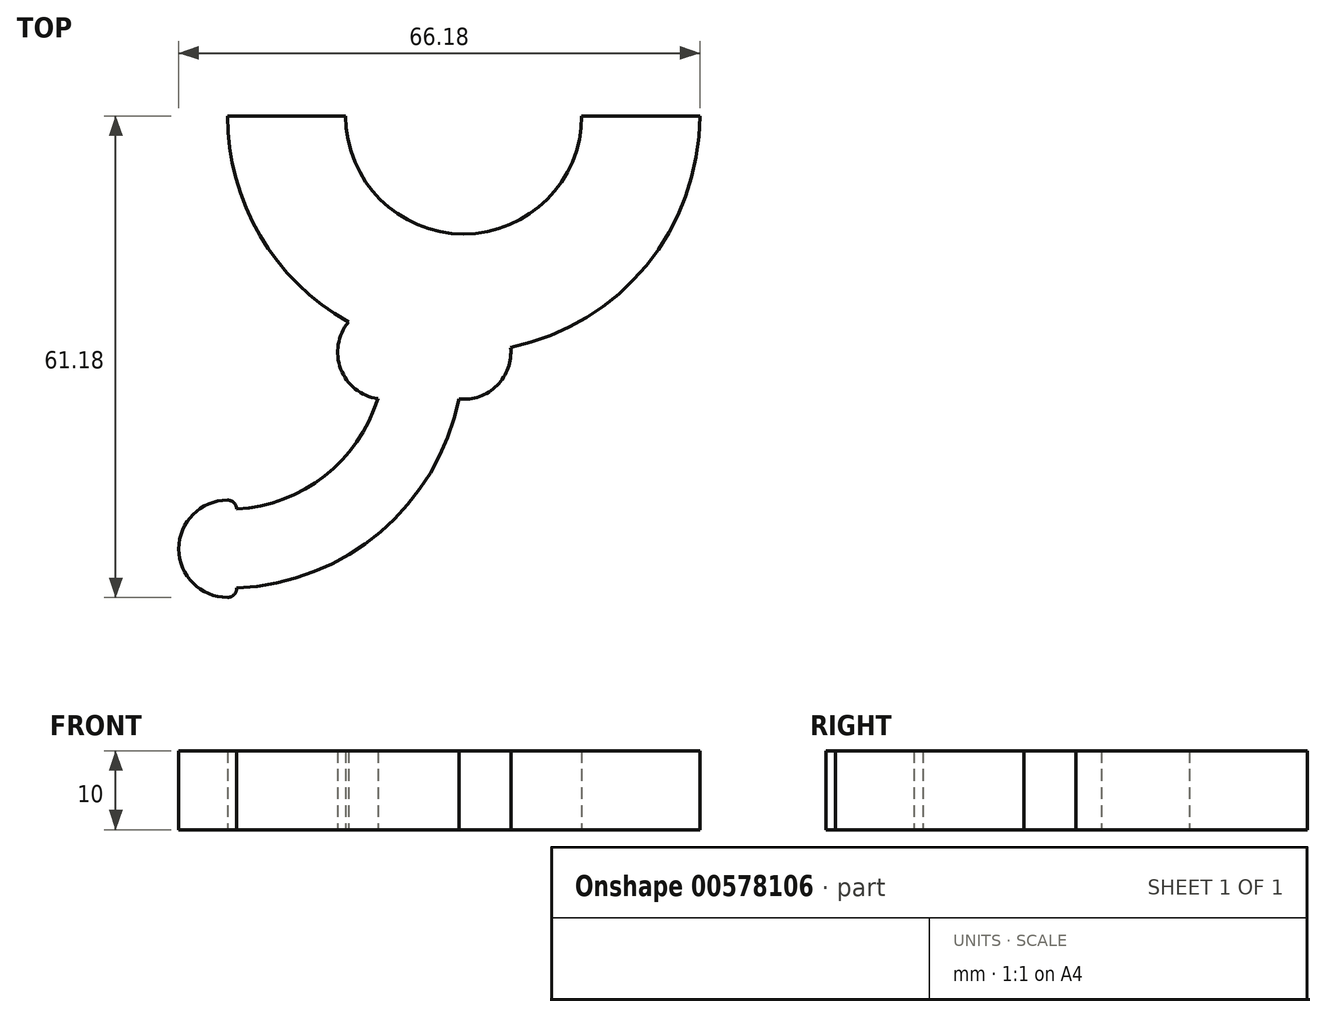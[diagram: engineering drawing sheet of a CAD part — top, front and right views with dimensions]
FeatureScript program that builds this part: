
annotation { "Feature Type Name" : "Feature", "Feature Type Description" : "" }
export const myFeature = defineFeature(function(context is Context, id is Id, definition is map)
    precondition{}
    {
        {
            var Q0;
            Q0=qCreatedBy(makeId("Top.planeOp"),FACE);
            var sketch = newSketch(context, id + "F0", { "sketchPlane" : qUnion([Q0])});
            skArc(sketch, "E0", {"start": v(15, 0) * mm, "mid": v(0, 15) * mm, "end": v(-15, 0) * mm});
            skLineSegment(sketch, "E1", {"start": v(30, 50) * mm, "end": v(30, 60) * mm});
            skLineSegment(sketch, "E2", {"start": v(30, 60) * mm, "end": v(30, 60) * mm});
            skArc(sketch, "E3", {"start": v(-5.97, 29.4) * mm, "mid": v(-23.23, 18.99) * mm, "end": v(-30, 0) * mm});
            skArc(sketch, "E4", {"start": v(30, 0) * mm, "mid": v(25.87, 15.18) * mm, "end": v(14.63, 26.19) * mm});
            skArc(sketch, "E5", {"start": v(28.82, 59.98) * mm, "mid": v(10.56, 52.85) * mm, "end": v(0.6, 35.97) * mm});
            skLineSegment(sketch, "E6", {"start": v(0, 30) * mm, "end": v(0, 30) * mm});
            skArc(sketch, "E7", {"start": v(28.82, 49.97) * mm, "mid": v(17.67, 45.75) * mm, "end": v(10.9, 35.93) * mm});
            skArc(sketch, "E8", {"start": v(4, 30) * mm, "mid": v(4, 29.87) * mm, "end": v(4, 29.73) * mm});
            skPoint(sketch, "E9.start.orphan", {"position": v(-28.8, -1.58) * mm});
            skArc(sketch, "E10.trimOffspring", {"start": v(0.6, 35.97) * mm, "mid": v(-4.24, 34.24) * mm, "end": v(-5.97, 29.4) * mm});
            skArc(sketch, "E11.trimOffspring", {"start": v(14.63, 26.19) * mm, "mid": v(15.6, 32.15) * mm, "end": v(10.9, 35.93) * mm});
            skArc(sketch, "E12", {"start": v(30, 48.82) * mm, "mid": v(36.18, 55) * mm, "end": v(30, 61.18) * mm});
            skArc(sketch, "E13", {"start": v(30, 61.18) * mm, "mid": v(29.16, 60.82) * mm, "end": v(28.82, 59.98) * mm});
            skArc(sketch, "E14", {"start": v(28.82, 49.97) * mm, "mid": v(29.18, 49.16) * mm, "end": v(30, 48.82) * mm});
            skLineSegment(sketch, "E15", {"start": v(-30, 0) * mm, "end": v(-15, 0) * mm});
            skLineSegment(sketch, "E16.trimOffspring", {"start": v(15, 0) * mm, "end": v(30, 0) * mm});
            skLineSegment(sketch, "E17.MirrorCS", {"start": v(0, -30) * mm, "end": v(0, -30) * mm});
            skLineSegment(sketch, "E18", {"start": v(-30, 0.02) * mm, "end": v(-15, 0.02) * mm});
            skLineSegment(sketch, "E19", {"start": v(15, 0.02) * mm, "end": v(30, 0.02) * mm});
            skArc(sketch, "E20.MirrorCS", {"start": v(-30, -61.16) * mm, "mid": v(-29.16, -60.8) * mm, "end": v(-28.82, -59.96) * mm});
            skArc(sketch, "E21.MirrorCS", {"start": v(-30, -48.8) * mm, "mid": v(-36.18, -54.98) * mm, "end": v(-30, -61.16) * mm});
            skArc(sketch, "E22.MirrorCS", {"start": v(-4, -29.98) * mm, "mid": v(-4, -29.85) * mm, "end": v(-4, -29.71) * mm});
            skArc(sketch, "E23.MirrorCS", {"start": v(-28.82, -49.95) * mm, "mid": v(-29.18, -49.14) * mm, "end": v(-30, -48.8) * mm});
            skLineSegment(sketch, "E24.MirrorCS", {"start": v(-30, -49.98) * mm, "end": v(-30, -59.98) * mm});
            skArc(sketch, "E25.MirrorCS", {"start": v(-0.6, -35.95) * mm, "mid": v(4.24, -34.22) * mm, "end": v(5.97, -29.38) * mm});
            skArc(sketch, "E26.MirrorCS", {"start": v(-30, 0.02) * mm, "mid": v(-25.87, -15.16) * mm, "end": v(-14.63, -26.17) * mm});
            skArc(sketch, "E27.MirrorCS", {"start": v(5.97, -29.38) * mm, "mid": v(23.23, -18.97) * mm, "end": v(30, 0.02) * mm});
            skArc(sketch, "E28.MirrorCS", {"start": v(-14.63, -26.17) * mm, "mid": v(-15.6, -32.13) * mm, "end": v(-10.9, -35.91) * mm});
            skArc(sketch, "E29.MirrorCS", {"start": v(-28.82, -49.95) * mm, "mid": v(-17.67, -45.73) * mm, "end": v(-10.9, -35.91) * mm});
            skArc(sketch, "E30.MirrorCS", {"start": v(-15, 0.02) * mm, "mid": v(0, -14.98) * mm, "end": v(15, 0.02) * mm});
            skArc(sketch, "E31.MirrorCS", {"start": v(-28.82, -59.96) * mm, "mid": v(-10.56, -52.83) * mm, "end": v(-0.6, -35.95) * mm});
            skSolve(sketch);
        }
        {
            var Q0;
            Q0=makeQuery(id+"F0.imprint","IMPRINT",FACE,{"disambiguationData":[TD([[makeQuery(id+"F0.imprint","IMPRINT",EDGE,{"derivedFrom":sQuery(id+"F0.wireOp",EDGE,"E4")}),1.0]])]});
            var Q1;
            {var subQ4=sQuery(id+"F0.wireOp",EDGE,"E15");Q1=makeQuery(id+"F0.imprint","IMPRINT",FACE,{"disambiguationData":[TD([[makeQuery(id+"F0.imprint","IMPRINT",EDGE,{"derivedFrom":subQ4}),-1.0]])]});}
            extrude(context, id + "F1", {"entities" : qUnion([Q0, Q1]), "depth" : 10 * mm, "offsetDistance" : 25 * mm});
        }
    });
